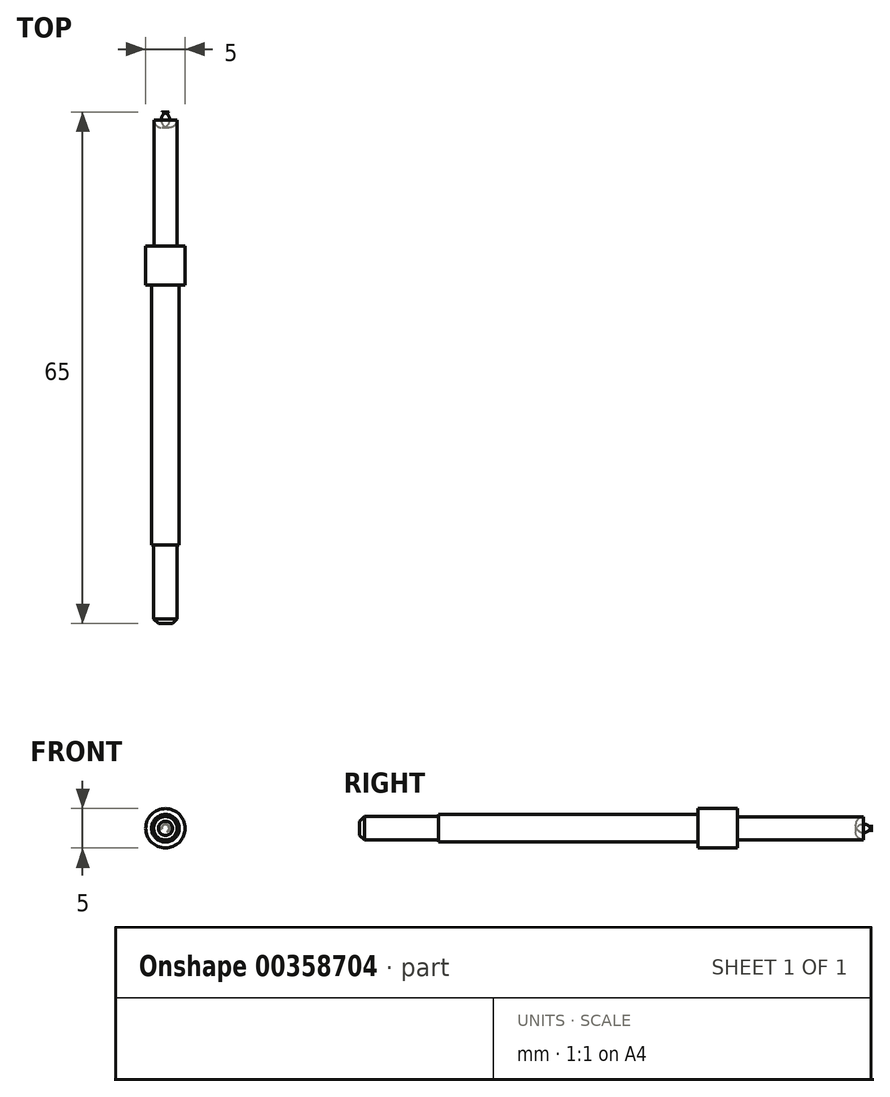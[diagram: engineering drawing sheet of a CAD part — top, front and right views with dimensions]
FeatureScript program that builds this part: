
annotation { "Feature Type Name" : "Feature", "Feature Type Description" : "" }
export const myFeature = defineFeature(function(context is Context, id is Id, definition is map)
    precondition{}
    {
        {
            var Q0;
            Q0=qCreatedBy(makeId("Right.planeOp"),FACE);
            var sketch = newSketch(context, id + "F0", { "sketchPlane" : qUnion([Q0])});
            skLineSegment(sketch, "E0", {"start": v(-47.48, 0) * mm, "end": v(17.52, 0) * mm});
            skLineSegment(sketch, "E1.0", {"start": v(-4.48, 2.5) * mm, "end": v(0.52, 2.5) * mm});
            skLineSegment(sketch, "E2", {"start": v(0.52, 1.45) * mm, "end": v(0.52, 2.5) * mm});
            skLineSegment(sketch, "E3.0", {"start": v(17.52, 0) * mm, "end": v(17.52, 0.45) * mm});
            skLineSegment(sketch, "E4.0", {"start": v(0.52, 1.45) * mm, "end": v(16.52, 1.45) * mm});
            skLineSegment(sketch, "E5.0", {"start": v(-37.48, 1.75) * mm, "end": v(-4.48, 1.75) * mm});
            skLineSegment(sketch, "E6.0", {"start": v(-4.48, 1.75) * mm, "end": v(-4.48, 2.5) * mm});
            skLineSegment(sketch, "E7", {"start": v(-47.48, 1.5) * mm, "end": v(-47.48, 0) * mm});
            skPoint(sketch, "E8.visualSharp", {"position": v(17.52, 1.45) * mm});
            skArc(sketch, "E8.filletArc", {"start": v(17.52, 0.45) * mm, "mid": v(17.22, 1.16) * mm, "end": v(16.52, 1.45) * mm});
            skLineSegment(sketch, "E9.0", {"start": v(-47.48, 1.5) * mm, "end": v(-37.48, 1.5) * mm});
            skLineSegment(sketch, "E10.0", {"start": v(-37.48, 1.75) * mm, "end": v(-37.48, 1.5) * mm});
            skSolve(sketch);
        }
        {
            var Q0;
            Q0=makeQuery(id+"F0.imprint","IMPRINT",FACE,{"disambiguationData":[TD([[makeQuery(id+"F0.imprint","IMPRINT",EDGE,{"derivedFrom":sQuery(id+"F0.wireOp",EDGE,"E0")}),1.0]])]});
            var Q1;
            Q1=sQuery(id+"F0.wireOp",EDGE,"E0");
            revolve(context, id + "F1", {"surfaceOperationType" : NewSurfaceOperationType.NEW, "entities" : qUnion([Q0]), "axis" : qUnion([Q1]), "revolveType" : RevolveType.FULL});
        }
        {
            var Q0;
            Q0=makeQuery(id+"F1.opRevolve","SWEPT_EDGE",EDGE,{"disambiguationData":[OSD([sQuery(id+"F0.wireOp",EDGE,"E7"),sQuery(id+"F0.wireOp",EDGE,"E9.0")])]});
            chamfer(context, id + "F2", {"entities" : qUnion([Q0]), "width" : 0.6 * mm, "tangentPropagation" : true});
        }
    });
